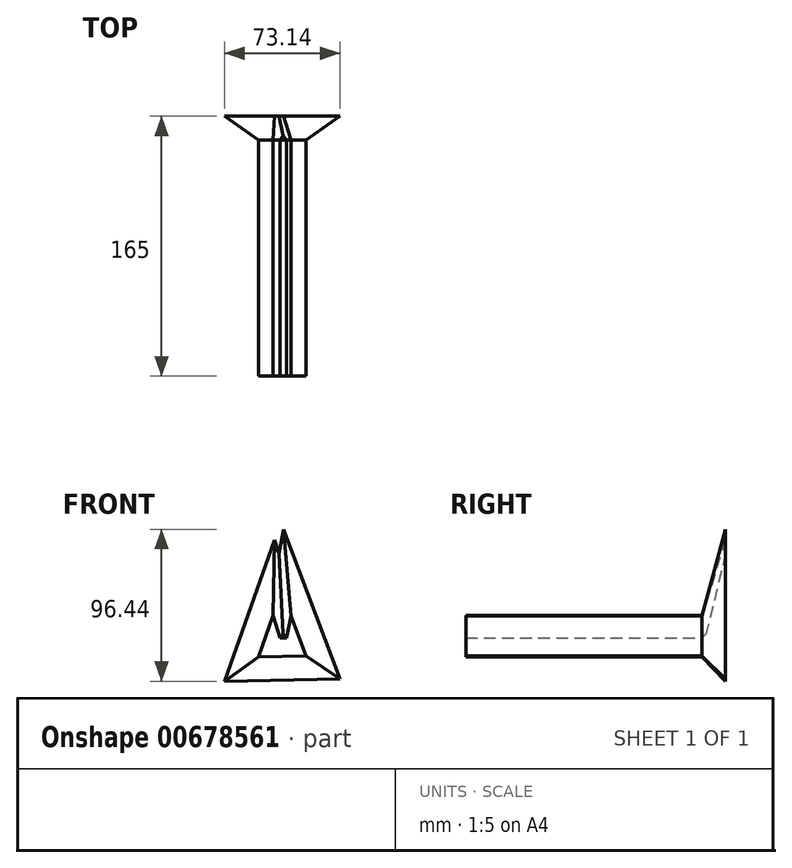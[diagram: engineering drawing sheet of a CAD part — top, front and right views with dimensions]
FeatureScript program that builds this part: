
annotation { "Feature Type Name" : "Feature", "Feature Type Description" : "" }
export const myFeature = defineFeature(function(context is Context, id is Id, definition is map)
    precondition{}
    {
        {
            var Q0;
            Q0=qCreatedBy(makeId("Front.planeOp"),FACE);
            var sketch = newSketch(context, id + "F0", { "sketchPlane" : qUnion([Q0])});
            skLineSegment(sketch, "E0", {"start": v(-33.58, 10.3) * mm, "end": v(-24.22, 36.7) * mm});
            skLineSegment(sketch, "E1", {"start": v(-24.22, 36.7) * mm, "end": v(-19.82, 22.26) * mm});
            skLineSegment(sketch, "E2", {"start": v(-19.82, 22.26) * mm, "end": v(-15.64, 22.26) * mm});
            skLineSegment(sketch, "E3", {"start": v(-15.64, 22.26) * mm, "end": v(-12.9, 36.38) * mm});
            skLineSegment(sketch, "E4", {"start": v(-12.9, 36.38) * mm, "end": v(-3.33, 10.92) * mm});
            skLineSegment(sketch, "E5", {"start": v(-3.33, 10.92) * mm, "end": v(-33.58, 10.3) * mm});
            skSolve(sketch);
        }
        {
            var Q0;
            Q0 = qSketchRegion(id + "F0", true);
            extrude(context, id + "F1", {"entities" : qUnion([Q0]), "depth" : 150 * mm, "offsetDistance" : 25 * mm});
        }
        {
            var Q0;
            Q0=makeQuery(id+"F1.opExtrude","CAP_FACE",FACE,{"disambiguationData":[OSD([sQuery(id+"F0.wireOp",EDGE,"E0"),sQuery(id+"F0.wireOp",EDGE,"E1"),sQuery(id+"F0.wireOp",EDGE,"E2"),sQuery(id+"F0.wireOp",EDGE,"E3"),sQuery(id+"F0.wireOp",EDGE,"E4"),sQuery(id+"F0.wireOp",EDGE,"E5")])],"isStart":true});
            var sketch = newSketch(context, id + "F2", { "sketchPlane" : qUnion([Q0])});
            skSolve(sketch);
        }
        {
            var Q0;
            Q0=makeQuery(id+"F2.imprint","IMPRINT",FACE,{"disambiguationData":[TD([[makeQuery(id+"F2.imprint","IMPRINT",EDGE,{"derivedFrom":makeQuery(id+"F1.opExtrude","CAP_EDGE",EDGE,{"disambiguationData":[OSD([sQuery(id+"F0.wireOp",EDGE,"E0")])],"isStart":true})}),1.0]])]});
            extrude(context, id + "F3", {"entities" : qUnion([Q0]), "operationType" : NewBodyOperationType.ADD, "depth" : 15 * mm, "offsetDistance" : 25 * mm, "hasDraft" : true, "draftAngle" : 45 * degree});
        }
    });
